# Revit family: lowbay-pc-reflector-80w_545098004100
name_source: partatom
category: Leuchten
revit_build: Autodesk Revit 2016 (Build: 20190508_0715(x64)
units: mm (PartAtom-declared; Revit-internal decimal feet)

## family parameters
Basisbauteil = Fläche
Beim Laden mit Abzugskörper schneiden = Nein
Bemaßung runder Anschluss = Durchmesser verwenden
Gemeinsam genutzt = Nein
Lichtquelle = Nein
Raumberechnungspunkt = Nein
Teiletyp = Normal

## types (1)
- Lowbay-PC-Reflector-80W (1 x LED, 8800 lm)
    Approval mark = CE
    Beschreibung = Transparent reflector, accessory for the Lowbay 80W.
    CIE Flux Codes = 52 84 95 98 100
    Height = 2608 mm
    Hersteller = OPPLE
    Lamp Light Flux = 8800 lm
    Lamp count = 1
    Lampe = 1 x LED
    Length = 421 mm
    Luminous efficacy = 110 lm/W
    ModVariant = Nein
    Modell = 545098004100
    Mounting Place = Ceiling
    Mounting Type = Pendant
    Number of Poles = 1
    OnlyDefault = Ja
    Power Factor = 1
    Product Name = Lowbay-PC-Reflector-80W
    Product group = Lowbay
    ProductGroupID = 915
    Protection Class = Protection class I
    Protection Degree = IP 20
    RLX_Detail_Level = 1
    RlxData = <blob elided: 26681 chars, md5=577f5ffe>
    Scheinlast = 80 VA
    Socket = socket
    Standby Power = 0 W
    System Light Flux = 8800 lm
    System Power = 80 W
    Typenbild = 545098004100.jpg
    Typenkommentare = Product without accessories
    URL = http://relux.com
    VarID = ---
    Voltage = 0 V
    Vorgabe-Ansicht = 1800 mm
    Weight = 0.00 kg
    Width = 0 mm  [stored 0 ft]

note: [stored X ft] marks values corroborated as IEEE doubles in the binary element streams (Revit-internal decimal feet)

## geometry (parser evidence)
native form markers: Blend x4, Sweep x12
no freeform markers — native parametric forms only
